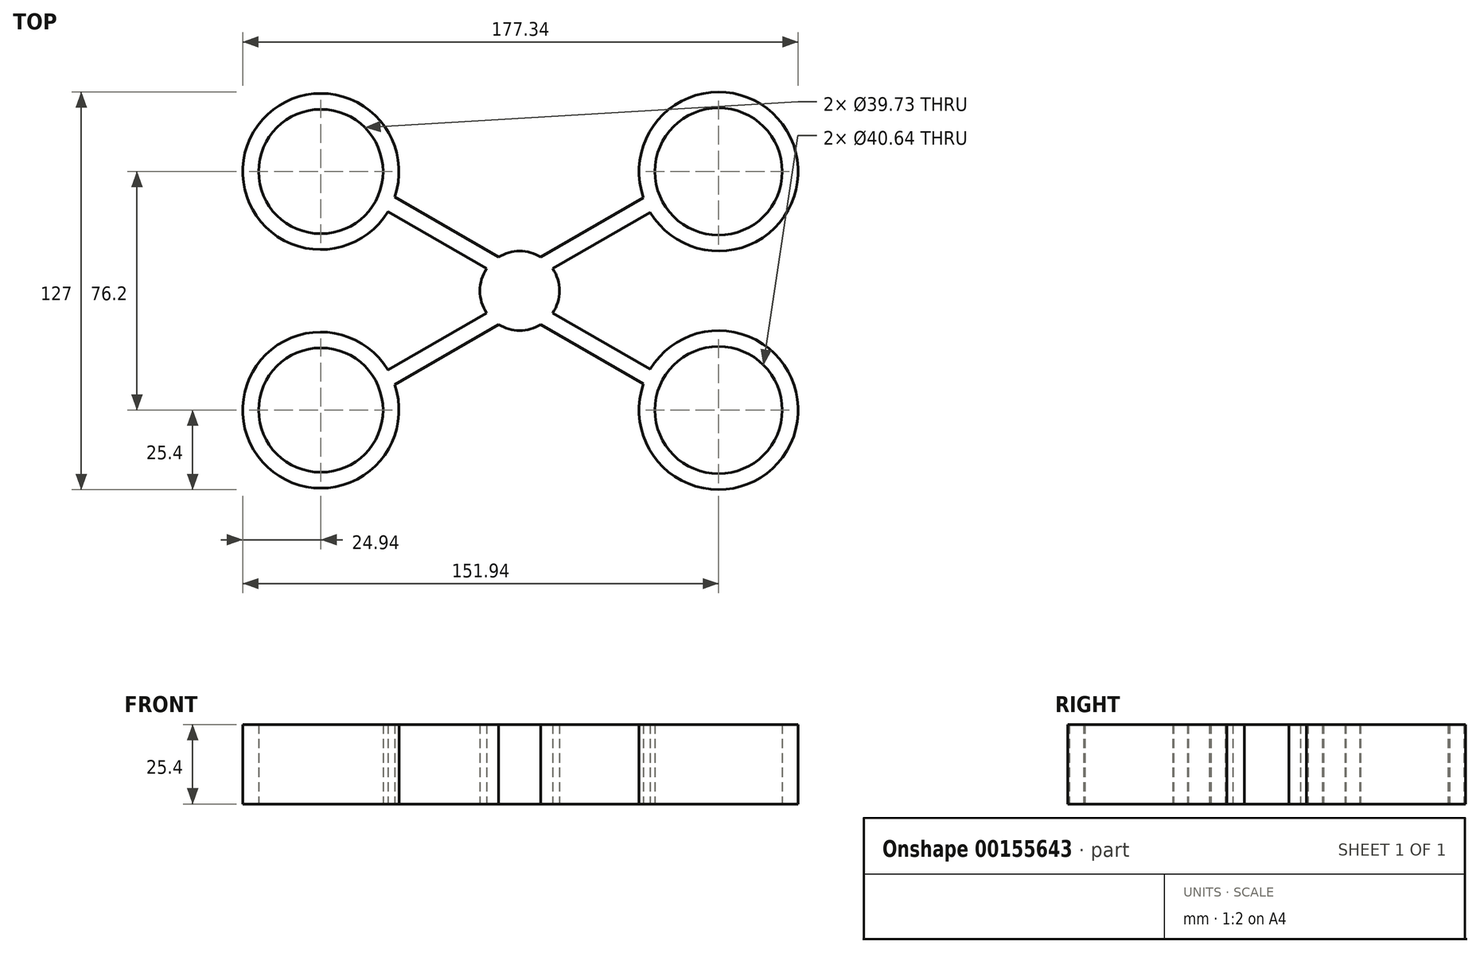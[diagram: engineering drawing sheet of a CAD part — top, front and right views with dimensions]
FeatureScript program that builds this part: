
annotation { "Feature Type Name" : "Feature", "Feature Type Description" : "" }
export const myFeature = defineFeature(function(context is Context, id is Id, definition is map)
    precondition{}
    {
        {
            var Q0;
            Q0=qCreatedBy(makeId("Top.planeOp"),FACE);
            var sketch = newSketch(context, id + "F0", { "sketchPlane" : qUnion([Q0])});
            skArc(sketch, "E0", {"start": v(-39.94, 29.92) * mm, "mid": v(-86.1, 48.65) * mm, "end": v(-42.1, 25.3) * mm});
            skArc(sketch, "E1", {"start": v(41.7, 25.07) * mm, "mid": v(86.5, 48.88) * mm, "end": v(39.53, 29.69) * mm});
            skCircle(sketch, "E2.0", {"center": v(-63.5, 38.1) * mm, "radius": 19.86 * mm});
            skCircle(sketch, "E3.0", {"center": v(63.5, 38.1) * mm, "radius": 20.32 * mm});
            skArc(sketch, "E4", {"start": v(12.7, 0) * mm, "mid": v(12.15, 3.7) * mm, "end": v(10.54, 7.1) * mm});
            skLineSegment(sketch, "E5", {"start": v(-39.94, 29.92) * mm, "end": v(-6.74, 10.77) * mm});
            skLineSegment(sketch, "E6.0", {"start": v(-42.1, 25.3) * mm, "end": v(-10.54, 7.1) * mm});
            skLineSegment(sketch, "E7.MirrorCS", {"start": v(39.53, 29.69) * mm, "end": v(6.74, 10.77) * mm});
            skLineSegment(sketch, "E8.MirrorCS", {"start": v(41.7, 25.07) * mm, "end": v(10.54, 7.1) * mm});
            skPoint(sketch, "E9.orphan", {"position": v(-16.56, 0) * mm});
            skPoint(sketch, "E10.orphan", {"position": v(-9.28, 6.37) * mm});
            skPoint(sketch, "E11.orphan", {"position": v(9.28, 6.37) * mm});
            skPoint(sketch, "E12.orphan", {"position": v(-42.48, 25.52) * mm});
            skArc(sketch, "E13.trimOffspring", {"start": v(-10.54, 7.1) * mm, "mid": v(-12.15, 3.7) * mm, "end": v(-12.7, 0) * mm});
            skArc(sketch, "E14.trimOffspring", {"start": v(6.74, 10.77) * mm, "mid": v(0, 12.7) * mm, "end": v(-6.74, 10.77) * mm});
            skPoint(sketch, "E15.orphan", {"position": v(42.48, 25.52) * mm});
            skArc(sketch, "E16.MirrorCS", {"start": v(-10.54, -7.1) * mm, "mid": v(-12.15, -3.7) * mm, "end": v(-12.7, 0) * mm});
            skArc(sketch, "E17.MirrorCS", {"start": v(12.7, 0) * mm, "mid": v(12.15, -3.7) * mm, "end": v(10.54, -7.1) * mm});
            skLineSegment(sketch, "E18.MirrorCS", {"start": v(41.7, -25.07) * mm, "end": v(10.54, -7.1) * mm});
            skPoint(sketch, "E19.MirrorP", {"position": v(-42.48, -25.52) * mm});
            skPoint(sketch, "E20.MirrorP", {"position": v(-9.28, -6.37) * mm});
            skArc(sketch, "E21.MirrorCS", {"start": v(6.74, -10.77) * mm, "mid": v(0, -12.7) * mm, "end": v(-6.74, -10.77) * mm});
            skPoint(sketch, "E22.MirrorP", {"position": v(9.28, -6.37) * mm});
            skArc(sketch, "E23.MirrorCS", {"start": v(41.7, -25.07) * mm, "mid": v(86.5, -48.88) * mm, "end": v(39.53, -29.69) * mm});
            skLineSegment(sketch, "E24.MirrorCS", {"start": v(39.53, -29.69) * mm, "end": v(6.74, -10.77) * mm});
            skPoint(sketch, "E25.MirrorP", {"position": v(42.48, -25.52) * mm});
            skCircle(sketch, "E26.MirrorC", {"center": v(-63.5, -38.1) * mm, "radius": 19.86 * mm});
            skArc(sketch, "E27.MirrorCS", {"start": v(-39.94, -29.92) * mm, "mid": v(-86.1, -48.65) * mm, "end": v(-42.1, -25.3) * mm});
            skLineSegment(sketch, "E28.MirrorCS", {"start": v(-42.1, -25.3) * mm, "end": v(-10.54, -7.1) * mm});
            skLineSegment(sketch, "E29.MirrorCS", {"start": v(-39.94, -29.92) * mm, "end": v(-6.74, -10.77) * mm});
            skCircle(sketch, "E30.MirrorC", {"center": v(63.5, -38.1) * mm, "radius": 20.32 * mm});
            skPoint(sketch, "E31.orphan", {"position": v(39.94, 29.92) * mm});
            skPoint(sketch, "E32.orphan", {"position": v(39.94, -29.92) * mm});
            skSolve(sketch);
        }
        {
            var Q0;
            Q0 = qSketchRegion(id + "F0", true);
            extrude(context, id + "F1", {"entities" : qUnion([Q0]), "depth" : 25.4 * mm});
        }
    });
